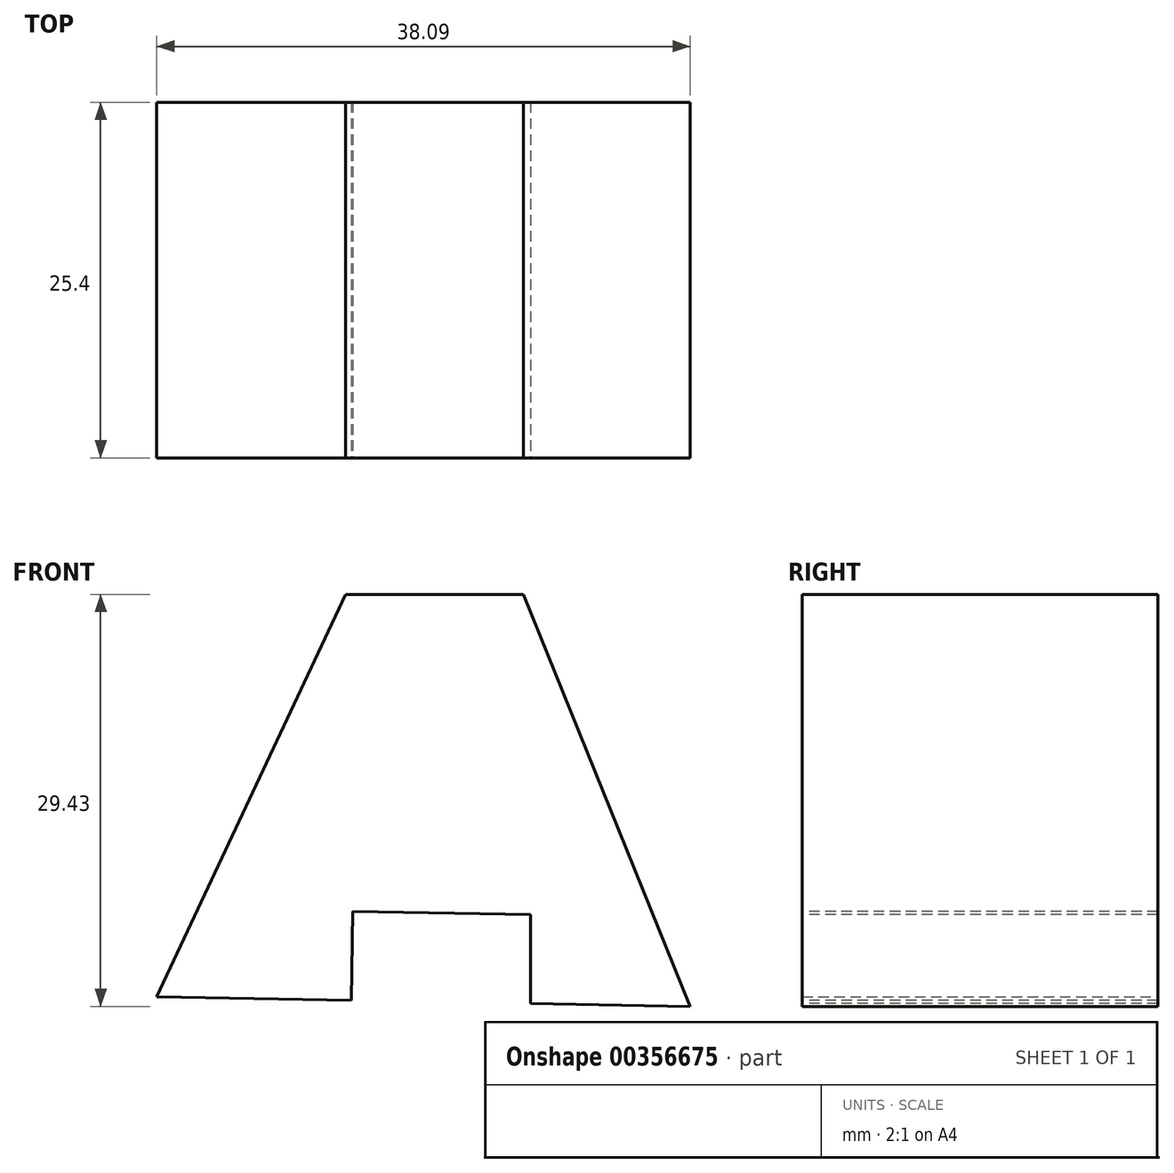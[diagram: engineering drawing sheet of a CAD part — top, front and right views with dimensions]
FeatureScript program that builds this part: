
annotation { "Feature Type Name" : "Feature", "Feature Type Description" : "" }
export const myFeature = defineFeature(function(context is Context, id is Id, definition is map)
    precondition{}
    {
        {
            var Q0;
            Q0=qCreatedBy(makeId("Front.planeOp"),FACE);
            var sketch = newSketch(context, id + "F0", { "sketchPlane" : qUnion([Q0])});
            skLineSegment(sketch, "E0", {"start": v(-7.21, -0.38) * mm, "end": v(6.26, 28.37) * mm});
            skLineSegment(sketch, "E1", {"start": v(6.26, 28.37) * mm, "end": v(18.96, 28.37) * mm});
            skLineSegment(sketch, "E2", {"start": v(18.96, 28.37) * mm, "end": v(30.88, -1.06) * mm});
            skLineSegment(sketch, "E3", {"start": v(30.88, -1.06) * mm, "end": v(-7.21, -0.38) * mm});
            skSolve(sketch);
        }
        {
            var Q0;
            Q0=makeQuery(id+"F0.imprint","IMPRINT",FACE,{"disambiguationData":[TD([[makeQuery(id+"F0.imprint","IMPRINT",EDGE,{"derivedFrom":sQuery(id+"F0.wireOp",EDGE,"E0")}),-1.0]])]});
            extrude(context, id + "F1", {"entities" : qUnion([Q0]), "depth" : 25.4 * mm});
        }
        {
            var Q0;
            Q0=makeQuery(id+"F1.opExtrude","CAP_FACE",FACE,{"disambiguationData":[OSD([sQuery(id+"F0.wireOp",EDGE,"E0"),sQuery(id+"F0.wireOp",EDGE,"E1"),sQuery(id+"F0.wireOp",EDGE,"E2"),sQuery(id+"F0.wireOp",EDGE,"E3")])],"isStart":false});
            var sketch = newSketch(context, id + "F2", { "sketchPlane" : qUnion([Q0])});
            skLineSegment(sketch, "E4", {"start": v(6.67, -0.63) * mm, "end": v(6.79, 5.72) * mm});
            skLineSegment(sketch, "E5", {"start": v(6.79, 5.72) * mm, "end": v(19.48, 5.5) * mm});
            skLineSegment(sketch, "E6", {"start": v(19.48, 5.5) * mm, "end": v(19.48, -0.86) * mm});
            skSolve(sketch);
        }
        {
            var Q0;
            {var subQ0=sQuery(id+"F2.wireOp",EDGE,"E4");Q0=makeQuery(id+"F2.imprint","IMPRINT",FACE,{"disambiguationData":[TD([[makeQuery(id+"F2.imprint","IMPRINT",EDGE,{"derivedFrom":subQ0}),-1.0]])]});}
            extrude(context, id + "F3", {"entities" : qUnion([Q0]), "operationType" : NewBodyOperationType.ADD, "depth" : 25.4 * mm});
        }
        {
            var Q0;
            Q0=makeQuery(id+"F3.opExtrude","CAP_FACE",FACE,{"disambiguationData":[OSD([sQuery(id+"F0.wireOp",EDGE,"E3"),sQuery(id+"F2.wireOp",EDGE,"E4"),sQuery(id+"F2.wireOp",EDGE,"E5"),sQuery(id+"F2.wireOp",EDGE,"E6")])],"isStart":false});
            extrude(context, id + "F4", {"entities" : qUnion([Q0]), "operationType" : NewBodyOperationType.REMOVE, "oppositeDirection" : true, "depth" : 50.8 * mm});
        }
    });
